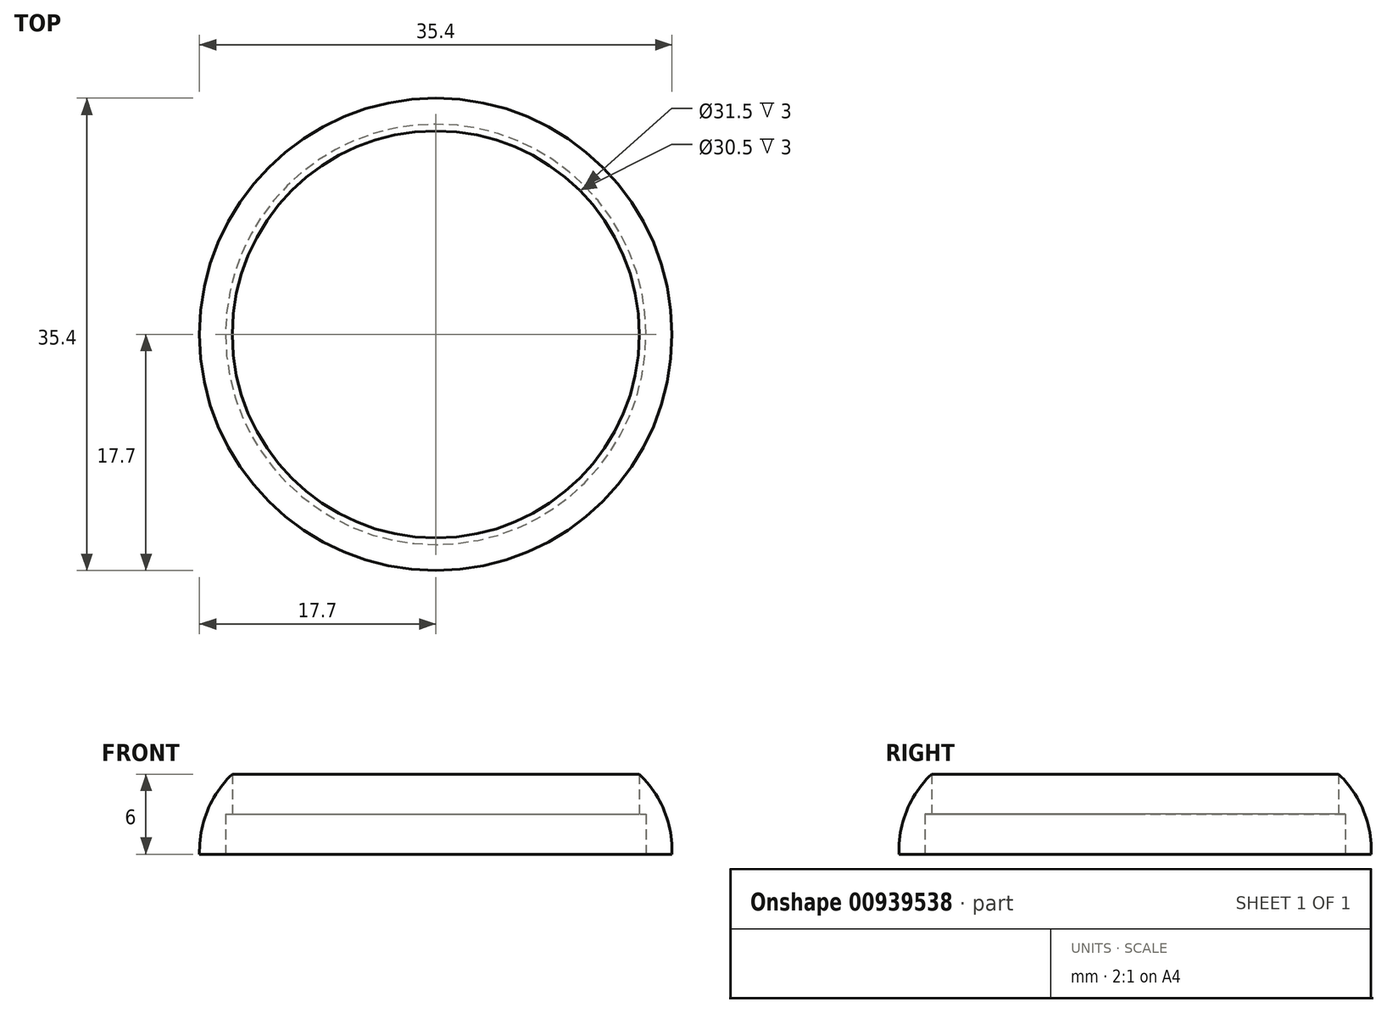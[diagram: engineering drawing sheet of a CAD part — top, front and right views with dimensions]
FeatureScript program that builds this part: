
annotation { "Feature Type Name" : "Feature", "Feature Type Description" : "" }
export const myFeature = defineFeature(function(context is Context, id is Id, definition is map)
    precondition{}
    {
        {
            var Q0;
            Q0=qCreatedBy(makeId("Top.planeOp"),FACE);
            var sketch = newSketch(context, id + "F0", { "sketchPlane" : qUnion([Q0])});
            skCircle(sketch, "E0", {"center": v(0, 0) * mm, "radius": 17.7 * mm});
            skSolve(sketch);
        }
        {
            var Q0;
            Q0=makeQuery(id+"F0.imprint","IMPRINT",FACE,{"disambiguationData":[TD([[makeQuery(id+"F0.imprint","IMPRINT",EDGE,{"derivedFrom":sQuery(id+"F0.wireOp",EDGE,"E0")}),1.0]])]});
            extrude(context, id + "F1", {"entities" : qUnion([Q0]), "depth" : 6 * mm, "offsetDistance" : 25 * mm});
        }
        {
            var Q0;
            Q0=makeQuery(id+"F1.opExtrude","CAP_FACE",FACE,{"disambiguationData":[OSD([sQuery(id+"F0.wireOp",EDGE,"E0")])],"isStart":true});
            var sketch = newSketch(context, id + "F2", { "sketchPlane" : qUnion([Q0])});
            skCircle(sketch, "E1", {"center": v(0, 0) * mm, "radius": 15.75 * mm});
            skSolve(sketch);
        }
        {
            var Q0;
            Q0=makeQuery(id+"F2.imprint","IMPRINT",FACE,{"disambiguationData":[TD([[makeQuery(id+"F2.imprint","IMPRINT",EDGE,{"derivedFrom":sQuery(id+"F2.wireOp",EDGE,"E1")}),1.0]])]});
            extrude(context, id + "F3", {"entities" : qUnion([Q0]), "operationType" : NewBodyOperationType.REMOVE, "oppositeDirection" : true, "depth" : 3 * mm, "offsetDistance" : 25 * mm});
        }
        {
            var Q0;
            Q0=makeQuery(id+"F3.boolean.opBoolean","COPY",FACE,{"derivedFrom":makeQuery(id+"F3.opExtrude","CAP_FACE",FACE,{"disambiguationData":[OSD([sQuery(id+"F2.wireOp",EDGE,"E1")])],"isStart":false})});
            var sketch = newSketch(context, id + "F4", { "sketchPlane" : qUnion([Q0])});
            skCircle(sketch, "E2", {"center": v(0, 0) * mm, "radius": 15.25 * mm});
            skSolve(sketch);
        }
        {
            var Q0;
            Q0=makeQuery(id+"F4.imprint","IMPRINT",FACE,{"disambiguationData":[TD([[makeQuery(id+"F4.imprint","IMPRINT",EDGE,{"derivedFrom":sQuery(id+"F4.wireOp",EDGE,"E2")}),1.0]])]});
            extrude(context, id + "F5", {"entities" : qUnion([Q0]), "operationType" : NewBodyOperationType.REMOVE, "oppositeDirection" : true, "depth" : 2 * mm, "offsetDistance" : 25 * mm});
        }
        {
            var Q0;
            Q0=makeQuery(id+"F1.opExtrude","CAP_FACE",FACE,{"disambiguationData":[OSD([sQuery(id+"F0.wireOp",EDGE,"E0")])],"isStart":false});
            var sketch = newSketch(context, id + "F6", { "sketchPlane" : qUnion([Q0])});
            skCircle(sketch, "E3", {"center": v(0, 0) * mm, "radius": 15.25 * mm});
            skSolve(sketch);
        }
        {
            var Q0;
            Q0=makeQuery(id+"F6.imprint","IMPRINT",FACE,{"disambiguationData":[TD([[makeQuery(id+"F6.imprint","IMPRINT",EDGE,{"derivedFrom":sQuery(id+"F6.wireOp",EDGE,"E3")}),1.0]])]});
            extrude(context, id + "F7", {"entities" : qUnion([Q0]), "operationType" : NewBodyOperationType.REMOVE, "oppositeDirection" : true, "depth" : 1 * mm, "offsetDistance" : 25 * mm});
        }
        {
            var Q0;
            Q0=makeQuery(id+"F1.opExtrude","CAP_EDGE",EDGE,{"disambiguationData":[OSD([sQuery(id+"F0.wireOp",EDGE,"E0")])],"isStart":false});
            fillet(context, id + "F8", {"entities" : qUnion([Q0]), "radius" : 8 * mm, "tangentPropagation" : true, "allowEdgeOverflow" : false});
        }
    });
